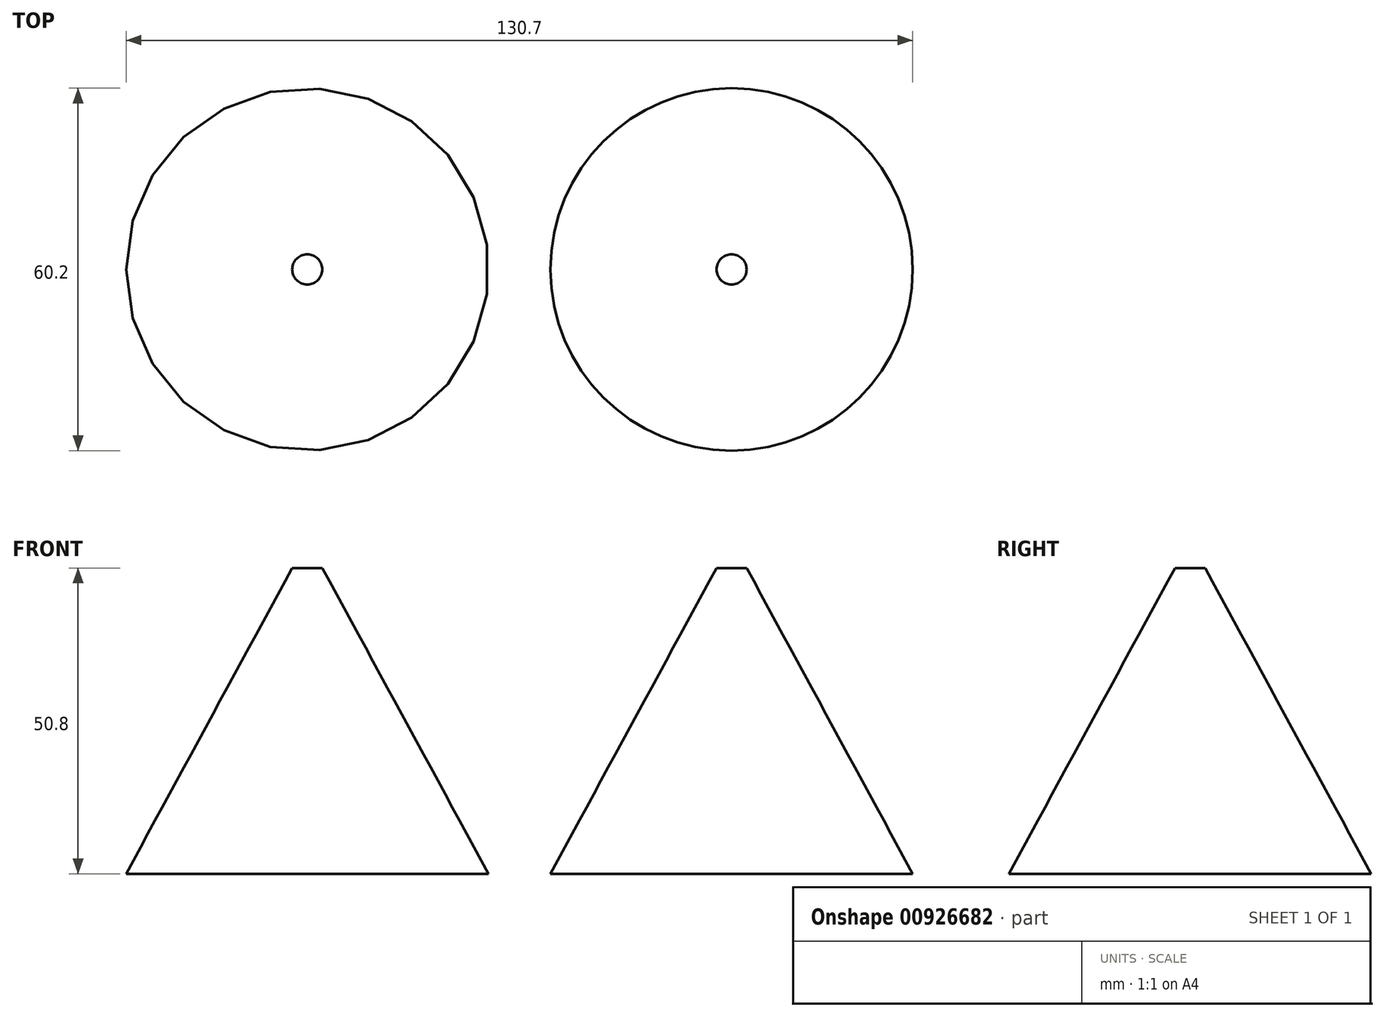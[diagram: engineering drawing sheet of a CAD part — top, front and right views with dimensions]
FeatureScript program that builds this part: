
annotation { "Feature Type Name" : "Feature", "Feature Type Description" : "" }
export const myFeature = defineFeature(function(context is Context, id is Id, definition is map)
    precondition{}
    {
        {
            var Q0;
            Q0=qCreatedBy(makeId("Top.planeOp"),FACE);
            var sketch = newSketch(context, id + "F0", { "sketchPlane" : qUnion([Q0])});
            skCircle(sketch, "E0", {"center": v(35.25, 0) * mm, "radius": 30.1 * mm});
            skSolve(sketch);
        }
        {
            assignVariable(context, id + "F1", {"name" : "offsetdistance", "anyValue" : 50.8 * mm});
        }
        {
            var Q0;
            Q0=qCreatedBy(makeId("Top.planeOp"),FACE);
            cPlane(context, id + "F2", {"entities" : qUnion([Q0]), "cplaneType" : CPlaneType.OFFSET, "offset" : getVariable(context, 'offsetdistance'), "width" : 150 * mm, "height" : 150 * mm});
        }
        {
            var Q0;
            Q0=qCreatedBy(id+"F2.planeOp",FACE);
            var sketch = newSketch(context, id + "F3", { "sketchPlane" : qUnion([Q0])});
            skCircle(sketch, "E1", {"center": v(35.26, 0) * mm, "radius": 2.5 * mm});
            skSolve(sketch);
        }
        {
            var Q0;
            Q0=makeQuery(id+"F0.imprint","IMPRINT",FACE,{"disambiguationData":[TD([[makeQuery(id+"F0.imprint","IMPRINT",EDGE,{"derivedFrom":sQuery(id+"F0.wireOp",EDGE,"E0")}),1.0]])]});
            var Q1;
            Q1=makeQuery(id+"F3.imprint","IMPRINT",FACE,{"disambiguationData":[TD([[makeQuery(id+"F3.imprint","IMPRINT",EDGE,{"derivedFrom":sQuery(id+"F3.wireOp",EDGE,"E1")}),1.0]])]});
            loft(context, id + "F4", {"sheetProfilesArray" : [{ "sheetProfileEntities" : qUnion([Q0]) }, { "sheetProfileEntities" : qUnion([Q1]) }]});
        }
        {
            var Q0;
            Q0=makeQuery(id+"F4.opLoft","SWEPT_BODY",BODY,{"disambiguationData":[OSD([makeQuery(id+"F0.imprint","IMPRINT",FACE,{"disambiguationData":[TD([[makeQuery(id+"F0.imprint","IMPRINT",EDGE,{"derivedFrom":sQuery(id+"F0.wireOp",EDGE,"E0")}),1.0]])]}),makeQuery(id+"F3.imprint","IMPRINT",FACE,{"disambiguationData":[TD([[makeQuery(id+"F3.imprint","IMPRINT",EDGE,{"derivedFrom":sQuery(id+"F3.wireOp",EDGE,"E1")}),1.0]])]})])]});
            var Q1;
            Q1=qCreatedBy(makeId("Right.planeOp"),FACE);
            mirror(context, id + "F5", {"entities" : qUnion([Q0]), "mirrorPlane" : qUnion([Q1])});
        }
    });
